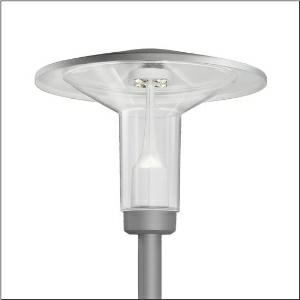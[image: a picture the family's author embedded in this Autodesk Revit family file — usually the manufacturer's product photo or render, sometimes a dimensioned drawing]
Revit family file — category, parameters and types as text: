
# Revit family: laterne_iq___pl1_2s_5xa5255jf14h000022_e294
name_source: partatom
category: Lighting Fixtures
units: mm (PartAtom-declared; Revit-internal decimal feet)

## family parameters
Cut with Voids When Loaded = No
Host = Face
Light Source = No
Part Type = Normal
Room Calculation Point = No
Round Connector Dimension = Use Diameter
Shared = No

## types (1)
- --- (1 x LED, 2970 lm, 19.3 W, 3000K)
    Apparent Load = 19 VA
    CIE Flux Codes = 25 63 94 98 100
    Color Rendering = 70
    Color Temperature = 3000K
    Default Elevation = 1800 mm
    Description = Lantern iQ, mast luminaire, Module 540 iQ-SR, primary light control with 3 zone facetted reflector, of plastic, silver coated, highly specular, structured, primary optical cover: cover, of PMMA, transparent, light distribution: PL1.2s, light emission: direct distribution, primary light characteristic: symmetric, installation type: post-top, LED, High Power LED, rated luminous flux: 2.970lm, luminous efficacy: 154lm/W, light colour: 730, colour temperature: 3000K, control gear: iQ Street-Remote, control: Street-Remote, Auto-Match, Temp-Guard, Lumen-Switch, Night-Set, Smart-Wire, Light-Fading, Desk-Remote (wireless, voltage-free reading and setting of iQ features in the workshop via application-optimized NFC function/RFID function), optimised constant luminous flux control (CLO 2.0), pre-setting: logarithmic dimming characteristic, mains connection: 230..240V, AC, 50/60Hz, connection cable pre-assembled, cable length: 5,5m, wiring characteristics: H07RN-F, start of lifetime: 19W, end of service life: 21W, reduction: 10W, luminaire housing, upper part, of glass-fibre reinforced polyester, coated, Siteco® metallic grey (DB 702S), diameter: 750mm, height: 583mm, spigot size: d x l = 76 x 70mm (post-top) | with reducer (optional accessory) 60 x 70mm, mounting height: 3..5m, post-top mast mounting element, of diecast aluminium, coated, Siteco® metallic grey (DB 702S), Module 540 iQ-SR, traffic white (RAL 9016), equipment: standard, protection rating (complete): IP65, insulation class (complete): insulation class II (safety insulation), certification: CE, ENEC, VDE, packaging unit: 1 piece

Light Distribution: PL1.2s
    Height = 583 mm
    Lamp = 1 x LED
    Lamp Light Flux = 2970 lm
    Lamp Power = 19.3 W
    Lamp count = 1
    Length = 750 mm
    Luminous efficacy = 154 lm/W
    Manufacturer = Siteco
    ModVariant = No
    Model = 5XA5255JF14H000022
    Number of Poles = 1
    OnlyDefault = Yes
    Power Factor = 1
    Product Name = Laterne iQ | PL1.2s
    Product group = mast luminaire | pylon top
    ProductGroupID = 6100
    Protection Class = Protection class II
    Protection Degree = IP 65
    RLX_Detail_Level = 1
    RLX_Emergency_Light_Flux = 0 lm
    RLX_Emergency_Type = 0
    RLX_Emergency_Type_DB = No
    RlxData = <blob elided: 31661 chars, md5=3bec1cc5>
    Socket = socket
    Standby Power = 0 W
    System Light Flux = 2970 lm
    System Power = 19 W
    Type Comments = factory setting: luminous flux: 100 % | dim-lin: 254 | 403 mA
    Type Image = l_1006050.jpg
    URL = http://relux.com
    VarID = @adj_167329
    Voltage = 0 V
    Weight = 0.00 kg
    Width = 0 mm  [stored 0 ft]

note: [stored X ft] marks values corroborated as IEEE doubles in the binary element streams (Revit-internal decimal feet)

## geometry (parser evidence)
native form markers: Blend x4, Sweep x10
no freeform markers — native parametric forms only
